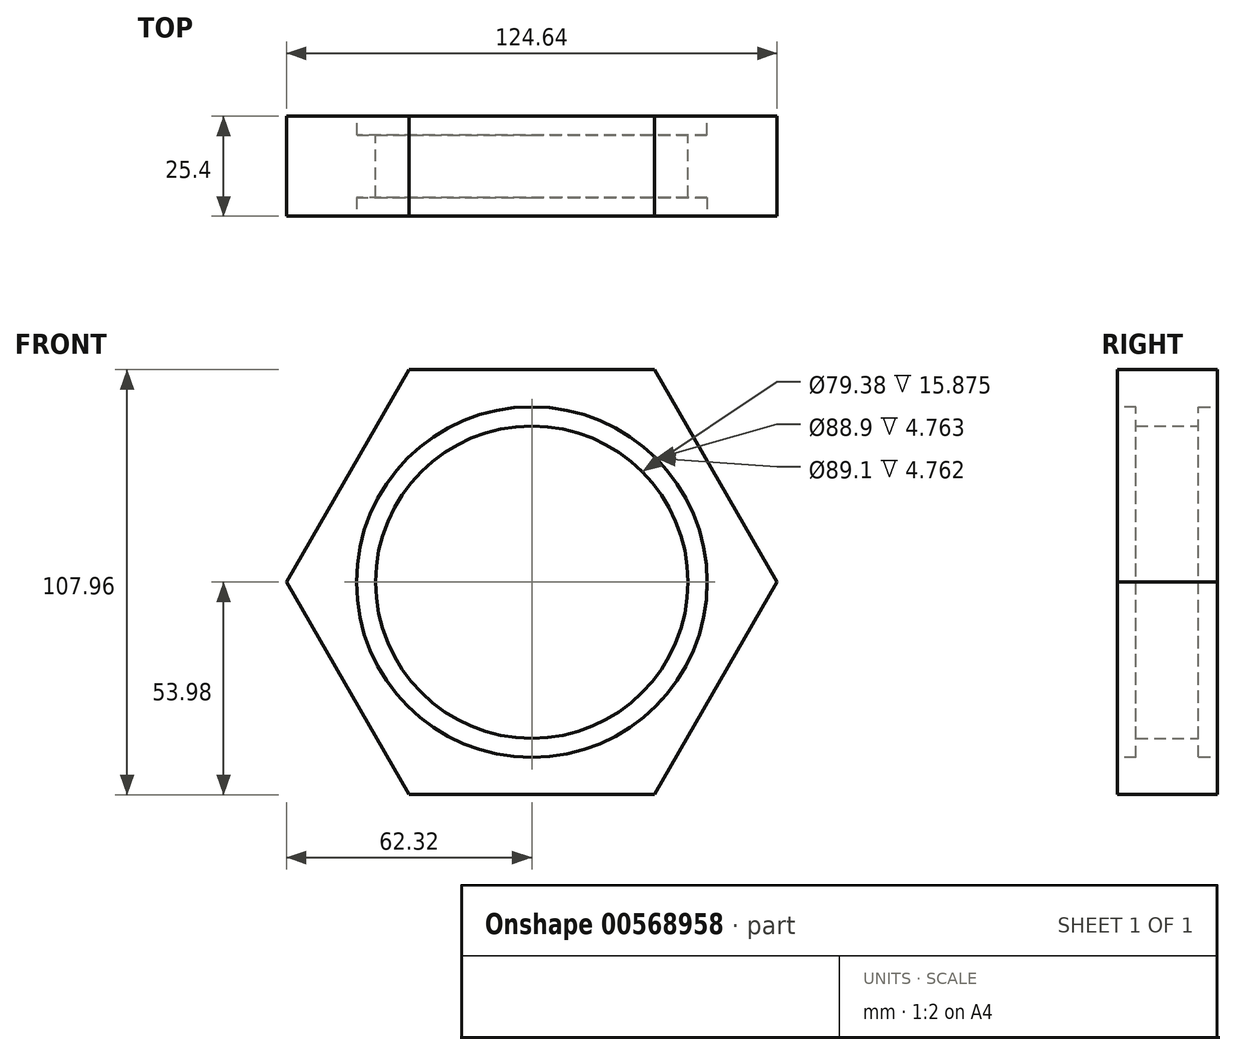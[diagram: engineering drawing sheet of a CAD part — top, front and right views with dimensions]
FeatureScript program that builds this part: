
annotation { "Feature Type Name" : "Feature", "Feature Type Description" : "" }
export const myFeature = defineFeature(function(context is Context, id is Id, definition is map)
    precondition{}
    {
        {
            var Q0;
            Q0=qCreatedBy(makeId("Front.planeOp"),FACE);
            var sketch = newSketch(context, id + "F0", { "sketchPlane" : qUnion([Q0])});
            skCircle(sketch, "E0.cCircle", {"center": v(0, 0) * mm, "radius": 53.98 * mm, "construction": true});
            skLineSegment(sketch, "E0.0", {"start": v(-31.16, 53.98) * mm, "end": v(31.16, 53.98) * mm});
            skLineSegment(sketch, "E0.1", {"start": v(31.16, 53.97) * mm, "end": v(62.32, 0) * mm});
            skLineSegment(sketch, "E0.2", {"start": v(62.32, 0) * mm, "end": v(31.16, -53.98) * mm});
            skLineSegment(sketch, "E0.3", {"start": v(31.16, -53.98) * mm, "end": v(-31.16, -53.98) * mm});
            skLineSegment(sketch, "E0.4", {"start": v(-31.16, -53.98) * mm, "end": v(-62.32, 0) * mm});
            skLineSegment(sketch, "E0.5", {"start": v(-62.32, 0) * mm, "end": v(-31.16, 53.98) * mm});
            skPoint(sketch, "E0.0.midPoint", {"position": v(0, 53.98) * mm});
            skCircle(sketch, "E1", {"center": v(0, 0) * mm, "radius": 39.69 * mm});
            skSolve(sketch);
        }
        {
            var Q0;
            Q0=makeQuery(id+"F0.imprint","IMPRINT",FACE,{"disambiguationData":[TD([[makeQuery(id+"F0.imprint","IMPRINT",EDGE,{"derivedFrom":sQuery(id+"F0.wireOp",EDGE,"E0.0")}),-1.0]])]});
            extrude(context, id + "F1", {"entities" : qUnion([Q0]), "depth" : 25.4 * mm, "offsetDistance" : 25.4 * mm});
        }
        {
            var Q0;
            Q0=qCreatedBy(makeId("Front.planeOp"),FACE);
            var sketch = newSketch(context, id + "F2", { "sketchPlane" : qUnion([Q0])});
            skCircle(sketch, "E2", {"center": v(0, 0) * mm, "radius": 44.45 * mm});
            skSolve(sketch);
        }
        {
            var Q0;
            Q0 = qSketchRegion(id + "F2", true);
            extrude(context, id + "F3", {"entities" : qUnion([Q0]), "operationType" : NewBodyOperationType.REMOVE, "depth" : 4.76 * mm, "offsetDistance" : 25.4 * mm});
        }
        {
            var Q0;
            Q0=makeQuery(id+"F1.opExtrude","CAP_FACE",FACE,{"disambiguationData":[OSD([sQuery(id+"F0.wireOp",EDGE,"E0.0"),sQuery(id+"F0.wireOp",EDGE,"E0.1"),sQuery(id+"F0.wireOp",EDGE,"E0.2"),sQuery(id+"F0.wireOp",EDGE,"E0.3"),sQuery(id+"F0.wireOp",EDGE,"E0.4"),sQuery(id+"F0.wireOp",EDGE,"E0.5"),sQuery(id+"F0.wireOp",EDGE,"E1")])],"isStart":false});
            var sketch = newSketch(context, id + "F4", { "sketchPlane" : qUnion([Q0])});
            skCircle(sketch, "E3", {"center": v(0, 0) * mm, "radius": 44.55 * mm});
            skSolve(sketch);
        }
        {
            var Q0;
            Q0=makeQuery(id+"F4.imprint","IMPRINT",FACE,{"disambiguationData":[TD([[makeQuery(id+"F4.imprint","IMPRINT",EDGE,{"derivedFrom":sQuery(id+"F4.wireOp",EDGE,"E3")}),1.0]])]});
            extrude(context, id + "F5", {"entities" : qUnion([Q0]), "operationType" : NewBodyOperationType.REMOVE, "oppositeDirection" : true, "depth" : 4.76 * mm, "offsetDistance" : 25.4 * mm});
        }
    });
